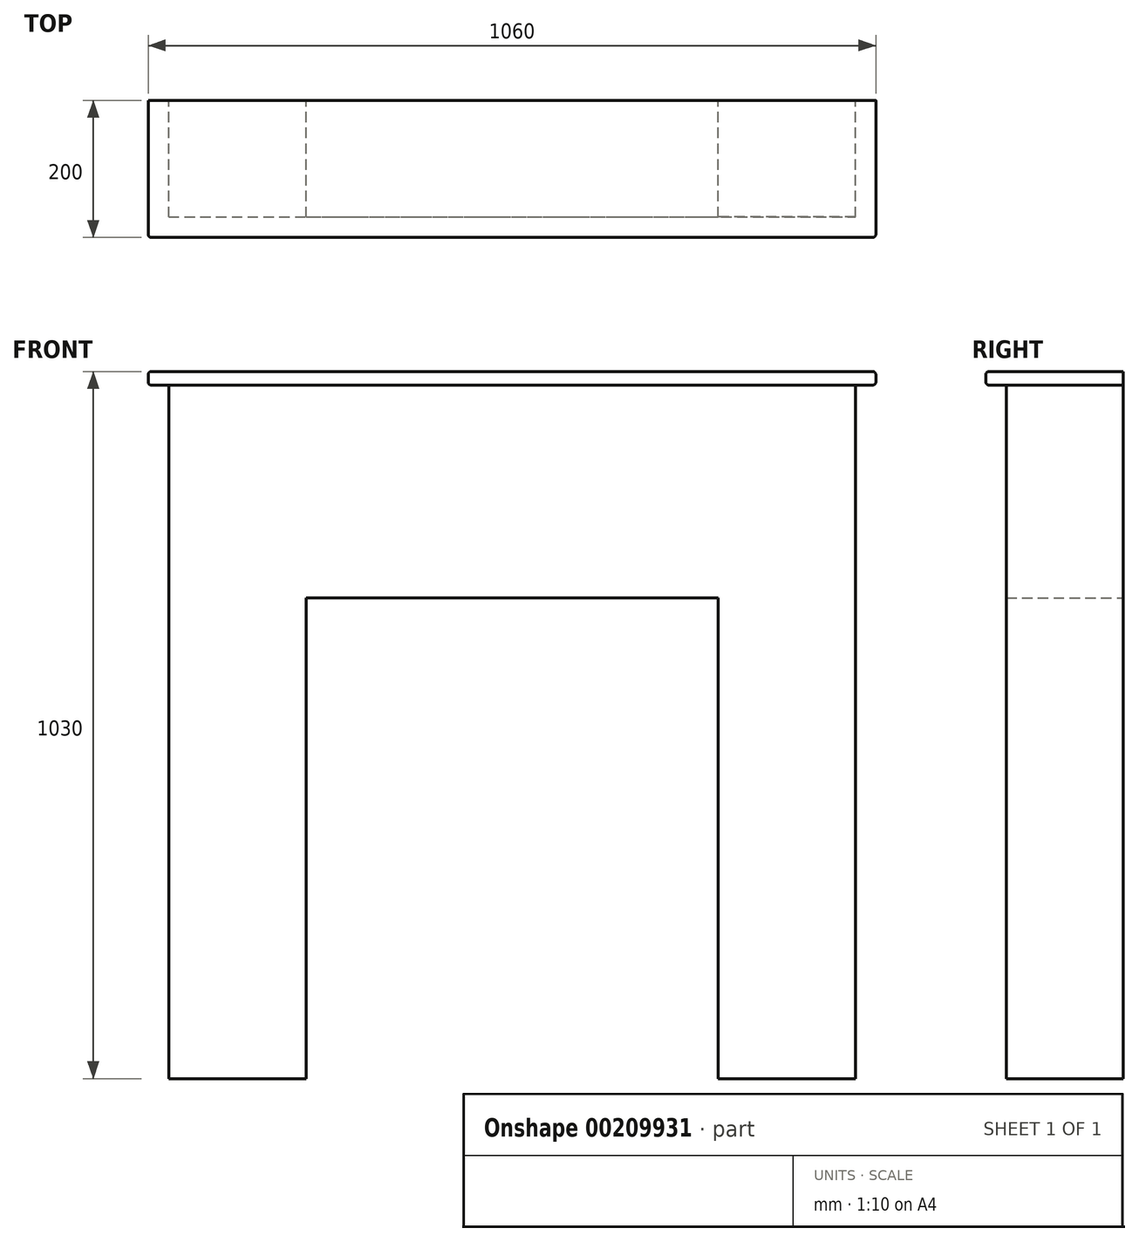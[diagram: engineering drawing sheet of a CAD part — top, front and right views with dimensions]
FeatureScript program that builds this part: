
annotation { "Feature Type Name" : "Feature", "Feature Type Description" : "" }
export const myFeature = defineFeature(function(context is Context, id is Id, definition is map)
    precondition{}
    {
        {
            var Q0;
            Q0=qCreatedBy(makeId("Front.planeOp"),FACE);
            var sketch = newSketch(context, id + "F0", { "sketchPlane" : qUnion([Q0])});
            skLineSegment(sketch, "E0", {"start": v(0, 1010) * mm, "end": v(-500, 1010) * mm});
            skLineSegment(sketch, "E1", {"start": v(-500, 1010) * mm, "end": v(-500, 0) * mm});
            skLineSegment(sketch, "E2", {"start": v(-500, 0) * mm, "end": v(-300, 0) * mm});
            skLineSegment(sketch, "E3", {"start": v(-300, 0) * mm, "end": v(-300, 700) * mm});
            skLineSegment(sketch, "E4", {"start": v(-300, 700) * mm, "end": v(0, 700) * mm});
            skLineSegment(sketch, "E5", {"start": v(0, 1010) * mm, "end": v(0, 0) * mm, "construction": true});
            skLineSegment(sketch, "E6.MirrorCS", {"start": v(0, 1010) * mm, "end": v(500, 1010) * mm});
            skLineSegment(sketch, "E7.MirrorCS", {"start": v(300, 700) * mm, "end": v(0, 700) * mm});
            skLineSegment(sketch, "E8.MirrorCS", {"start": v(300, 0) * mm, "end": v(300, 700) * mm});
            skLineSegment(sketch, "E9.MirrorCS", {"start": v(500, 0) * mm, "end": v(300, 0) * mm});
            skLineSegment(sketch, "E10.MirrorCS", {"start": v(500, 1010) * mm, "end": v(500, 0) * mm});
            skSolve(sketch);
        }
        {
            var Q0;
            Q0=makeQuery(id+"F0.imprint","IMPRINT",FACE,{"disambiguationData":[TD([[makeQuery(id+"F0.imprint","IMPRINT",EDGE,{"derivedFrom":sQuery(id+"F0.wireOp",EDGE,"E0")}),1.0]])]});
            extrude(context, id + "F1", {"entities" : qUnion([Q0]), "depth" : 170 * mm});
        }
        {
            var Q0;
            Q0=makeQuery(id+"F1.opExtrude","SWEPT_FACE",FACE,{"disambiguationData":[OSD([sQuery(id+"F0.wireOp",EDGE,"E0"),sQuery(id+"F0.wireOp",EDGE,"E6.MirrorCS")])]});
            var sketch = newSketch(context, id + "F2", { "sketchPlane" : qUnion([Q0])});
            skLineSegment(sketch, "E11.bottom", {"start": v(-530, 0) * mm, "end": v(530, 0) * mm});
            skLineSegment(sketch, "E11.top", {"start": v(-530, -200) * mm, "end": v(530, -200) * mm});
            skLineSegment(sketch, "E11.left", {"start": v(-530, 0) * mm, "end": v(-530, -200) * mm});
            skLineSegment(sketch, "E11.right", {"start": v(530, 0) * mm, "end": v(530, -200) * mm});
            skSolve(sketch);
        }
        {
            var Q0;
            Q0 = qSketchRegion(id + "F2", true);
            extrude(context, id + "F3", {"entities" : qUnion([Q0]), "operationType" : NewBodyOperationType.ADD, "depth" : 20 * mm});
        }
        {
            var Q0;
            Q0=makeQuery(id+"F3.opExtrude","CAP_EDGE",EDGE,{"disambiguationData":[OSD([sQuery(id+"F2.wireOp",EDGE,"E11.top")])],"isStart":true});
            fillet(context, id + "F4", {"entities" : qUnion([Q0]), "radius" : 5 * mm, "tangentPropagation" : true, "allowEdgeOverflow" : false});
        }
        {
            var Q0;
            Q0=makeQuery(id+"F3.opExtrude","CAP_EDGE",EDGE,{"disambiguationData":[OSD([sQuery(id+"F2.wireOp",EDGE,"E11.top")])],"isStart":false});
            fillet(context, id + "F5", {"entities" : qUnion([Q0]), "radius" : 5 * mm, "tangentPropagation" : true, "allowEdgeOverflow" : false});
        }
        {
            var Q0;
            Q0=makeQuery(id+"F3.opExtrude","CAP_EDGE",EDGE,{"disambiguationData":[OSD([sQuery(id+"F2.wireOp",EDGE,"E11.right")])],"isStart":false});
            fillet(context, id + "F6", {"entities" : qUnion([Q0]), "radius" : 5 * mm, "tangentPropagation" : true, "allowEdgeOverflow" : false});
        }
        {
            var Q0;
            Q0=makeQuery(id+"F3.opExtrude","CAP_EDGE",EDGE,{"disambiguationData":[OSD([sQuery(id+"F2.wireOp",EDGE,"E11.left")])],"isStart":false});
            fillet(context, id + "F7", {"entities" : qUnion([Q0]), "radius" : 5 * mm, "tangentPropagation" : true, "allowEdgeOverflow" : false});
        }
    });
